# Revit family: LAMP_KOMBIC 100 SURFACE SUSPENDED TRACK 2000 CRI80 OPAL
name_source: partatom
category: Luminarias
revit_build: Autodesk Revit 2018 (Build: 20190510_1515(x64)
units: mm (PartAtom-declared; Revit-internal decimal feet)

## family parameters
Anfitrión = Cara
Compartido = No
Corte con vacíos al cargar = No
Cota de conector redondo = Diámetro de uso
Origen de luz = Sí
Punto de cálculo de habitación = No
Tipo de pieza = Normal

## types (12) — shared parameters
CRI = 80
Cambio de temperatura de color de luz atenuada = <Ninguno>
Diameter = 100 mm  [stored 0.328084 ft]
Elevación por defecto = 1219 mm
Fabricante = LAMP
Filtro de color = 16777215
Gear = Electronic
Height = 120 mm  [stored 0.393701 ft]
IEE = A+
Installation instructions = https://www.lamp.es
Insulation class = I
LED Lifetime = 50.000 L80 B10
Lamp = COB LED
Last update = 28/07/2021
Luminaire type = Track Suspended
MacAdam = 3
Manufacturer URL = http://www.lamp.es
Manufacturer country = Spain
Manufacturer name = LAMP
Material cable suspension = LAMP_Acero genérico
Material difusor = LAMP_PMMA Difusor Kombic
Material floron = LAMP_Plástico genérico NG
Model explanation = Possibility to modify the lenght of the suspension cable up to 1m
Power = 12 W
Power Supply = 220-240V 50/60Hz
Product URL = https://www.lamp.es
Product datasheet = http://www.lamp.es
Protection rating = IP40
Type = COB PHILIPS
Weight = 0.50 kg
Ángulo de inclinación = -90.00°

## per-type parameters (varying)
| type | Archivo de red fotométrica | Efficacy | Finish | Material cuerpo | Material reflector | Modelo | Plum | Product code |
| 1392LM 3000K  M/B | K11rd2040OP830NMw.IES | 104 lm/W | Matte black RAL 9011 | LAMP_Plástico genérico NG | LAMP_PC Reflector Kombic Metalizado Mate | K11ST2040OP830NMB | 13 W | K11ST2040OP830NMB |
| 1392LM 3000K  M/W | K11rd2040OP830NMW.IES | 104 lm/W | Matte Traffic white RAL 9016 | LAMP_Plástico genérico BL | LAMP_PC Reflector Kombic Metalizado Mate | K11ST2040OP830NMW | 13 W | K11ST2040OP830NMW |
| 1454LM 3000K  W/B | K11rd2040OP830NWw.IES | 109 lm/W | Matte black RAL 9011 | LAMP_Plástico genérico NG | LAMP_PC Reflector Kombic Blanco | K11ST2040OP830NWB | 13 W | K11ST2040OP830NWB |
| 1454LM 3000K  W/W | K11rd2040OP830NWW.IES | 109 lm/W | Matte Traffic white RAL 9016 | LAMP_Plástico genérico BL | LAMP_PC Reflector Kombic Blanco | K11ST2040OP830NWW | 13 W | K11ST2040OP830NWW |
| 1460LM 3000K  BR/B | K11rd2040OP830NRw.IES | 107 lm/W | Matte black RAL 9011 | LAMP_Plástico genérico NG | LAMP_PC Reflector Kombic Metalizado Brillante | K11ST2040OP830NRB | 14 W | K11ST2040OP830NRB |
| 1460LM 3000K  BR/W | K11rd2040OP830NRW.IES | 107 lm/W | Matte Traffic white RAL 9016 | LAMP_Plástico genérico BL | LAMP_PC Reflector Kombic Metalizado Brillante | K11ST2040OP830NRW | 14 W | K11ST2040OP830NRW |
| 1474LM 4000K  M/B | K11rd2040OP840NMw.IES | 110 lm/W | Matte black RAL 9011 | LAMP_Plástico genérico NG | LAMP_PC Reflector Kombic Metalizado Mate | K11ST2040OP840NMB | 13 W | K11ST2040OP840NMB |
| 1474LM 4000K  M/W | K11rd2040OP840NMW.IES | 110 lm/W | Matte Traffic white RAL 9016 | LAMP_Plástico genérico BL | LAMP_PC Reflector Kombic Metalizado Mate | K11ST2040OP840NMW | 13 W | K11ST2040OP840NMW |
| 1541LM 4000K  W/B | K11rd2040OP840NWw.IES | 115 lm/W | Matte black RAL 9011 | LAMP_Plástico genérico NG | LAMP_PC Reflector Kombic Blanco | K11ST2040OP840NWB | 13 W | K11ST2040OP840NWB |
| 1541LM 4000K  W/W | K11rd2040OP840NWW.IES | 115 lm/W | Matte Traffic white RAL 9016 | LAMP_Plástico genérico BL | LAMP_PC Reflector Kombic Blanco | K11ST2040OP840NWW | 13 W | K11ST2040OP840NWW |
| 1547LM 4000K  BR/B | K11rd2040OP840NRw.IES | 115 lm/W | Matte black RAL 9011 | LAMP_Plástico genérico NG | LAMP_PC Reflector Kombic Metalizado Brillante | K11ST2040OP840NRB | 13 W | K11ST2040OP840NRB |
| 1547LM 4000K  BR/W | K11rd2040OP840NRW.IES | 115 lm/W | Matte Traffic white RAL 9016 | LAMP_Plástico genérico BL | LAMP_PC Reflector Kombic Metalizado Brillante | K11ST2040OP840NRW | 13 W | K11ST2040OP840NRW |

note: [stored X ft] marks values corroborated as IEEE doubles in the binary element streams (Revit-internal decimal feet)
